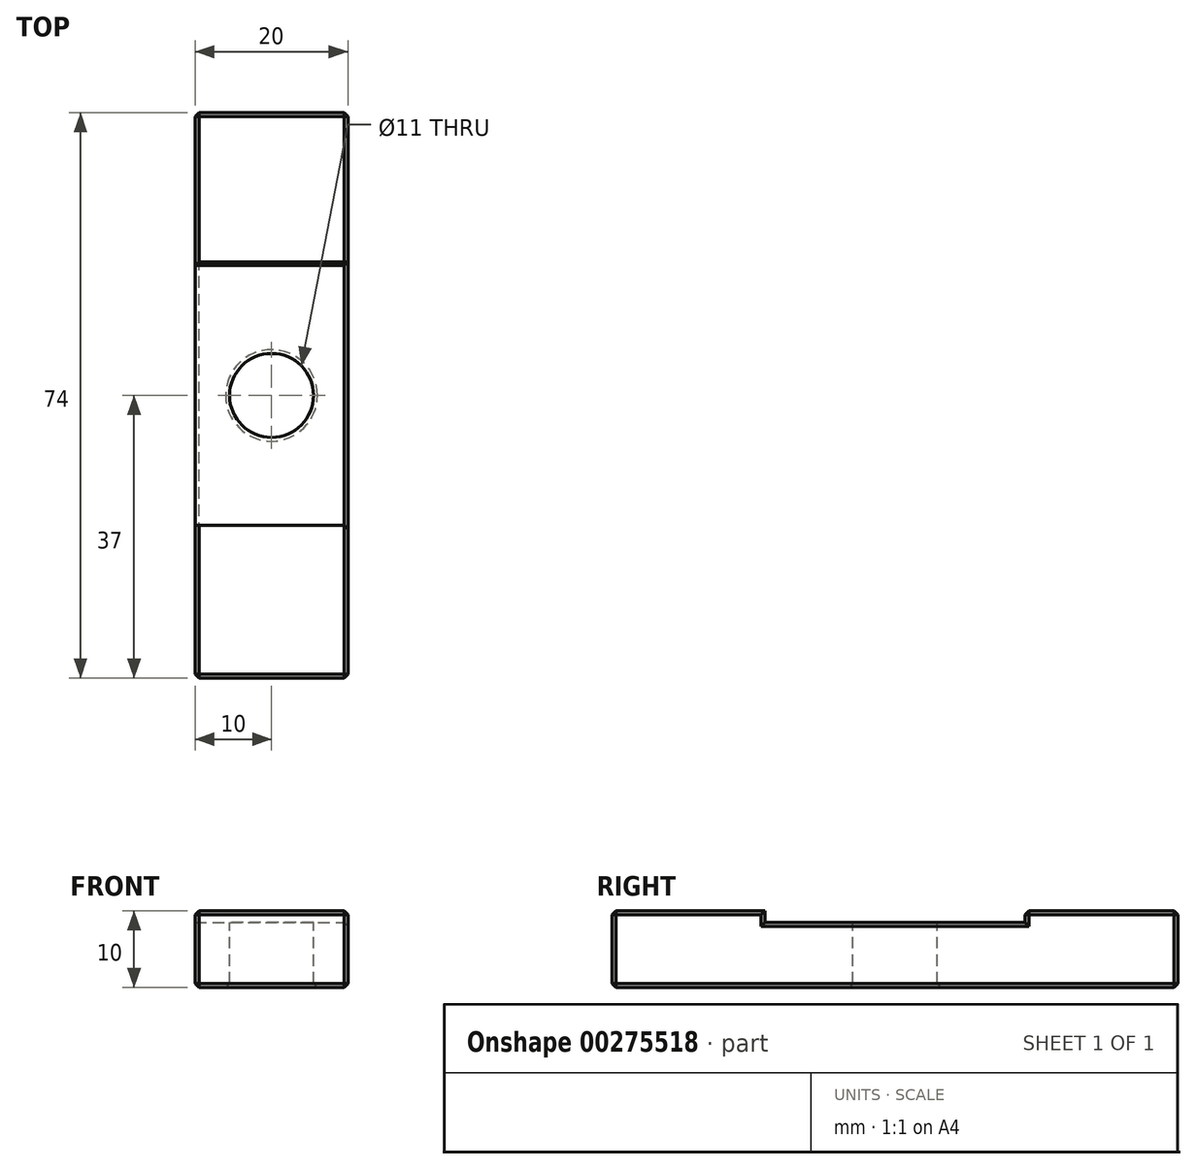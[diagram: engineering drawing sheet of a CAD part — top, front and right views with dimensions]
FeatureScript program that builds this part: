
annotation { "Feature Type Name" : "Feature", "Feature Type Description" : "" }
export const myFeature = defineFeature(function(context is Context, id is Id, definition is map)
    precondition{}
    {
        {
            var Q0;
            Q0=qCreatedBy(makeId("Top.planeOp"),FACE);
            var sketch = newSketch(context, id + "F0", { "sketchPlane" : qUnion([Q0])});
            skLineSegment(sketch, "E0.bottom", {"start": v(-10, -37) * mm, "end": v(10, -37) * mm});
            skLineSegment(sketch, "E0.top", {"start": v(-10, 37) * mm, "end": v(10, 37) * mm});
            skLineSegment(sketch, "E0.left", {"start": v(-10, -37) * mm, "end": v(-10, 37) * mm});
            skLineSegment(sketch, "E0.right", {"start": v(10, -37) * mm, "end": v(10, 37) * mm});
            skPoint(sketch, "E0.middle", {"position": v(0, 0) * mm});
            skSolve(sketch);
        }
        {
            var Q0;
            Q0 = qSketchRegion(id + "F0", true);
            extrude(context, id + "F1", {"entities" : qUnion([Q0]), "depth" : 10 * mm});
        }
        {
            var Q0;
            Q0=makeQuery(id+"F1.opExtrude","CAP_FACE",FACE,{"disambiguationData":[OSD([sQuery(id+"F0.wireOp",EDGE,"E0.bottom"),sQuery(id+"F0.wireOp",EDGE,"E0.top"),sQuery(id+"F0.wireOp",EDGE,"E0.left"),sQuery(id+"F0.wireOp",EDGE,"E0.right")])],"isStart":false});
            var sketch = newSketch(context, id + "F2", { "sketchPlane" : qUnion([Q0])});
            skLineSegment(sketch, "E1.bottom", {"start": v(-10, 37) * mm, "end": v(10, 37) * mm});
            skLineSegment(sketch, "E1.top", {"start": v(-10, 17) * mm, "end": v(10, 17) * mm});
            skLineSegment(sketch, "E1.left", {"start": v(-10, 37) * mm, "end": v(-10, 17) * mm});
            skLineSegment(sketch, "E1.right", {"start": v(10, 37) * mm, "end": v(10, 17) * mm});
            skLineSegment(sketch, "E2.bottom", {"start": v(10, -37) * mm, "end": v(-10, -37) * mm});
            skLineSegment(sketch, "E2.top", {"start": v(10, -17) * mm, "end": v(-10, -17) * mm});
            skLineSegment(sketch, "E2.left", {"start": v(10, -37) * mm, "end": v(10, -17) * mm});
            skLineSegment(sketch, "E2.right", {"start": v(-10, -37) * mm, "end": v(-10, -17) * mm});
            skSolve(sketch);
        }
        {
            var Q0;
            {var subQ0=sQuery(id+"F2.wireOp",EDGE,"E1.top");Q0=makeQuery(id+"F2.imprint","IMPRINT",FACE,{"disambiguationData":[TD([[makeQuery(id+"F2.imprint","IMPRINT",EDGE,{"derivedFrom":subQ0}),-1.0]])]});}
            extrude(context, id + "F3", {"entities" : qUnion([Q0]), "operationType" : NewBodyOperationType.REMOVE, "oppositeDirection" : true, "depth" : 1.5 * mm});
        }
        {
            var Q0;
            Q0=makeQuery(id+"F3.boolean.opBoolean","COPY",FACE,{"derivedFrom":makeQuery(id+"F3.opExtrude","CAP_FACE",FACE,{"disambiguationData":[OSD([sQuery(id+"F0.wireOp",EDGE,"E0.left"),sQuery(id+"F0.wireOp",EDGE,"E0.right"),sQuery(id+"F2.wireOp",EDGE,"E1.top"),sQuery(id+"F2.wireOp",EDGE,"E2.top")])],"isStart":false})});
            var sketch = newSketch(context, id + "F4", { "sketchPlane" : qUnion([Q0])});
            skCircle(sketch, "E3", {"center": v(0, 0) * mm, "radius": 5.5 * mm});
            skSolve(sketch);
        }
        {
            var Q0;
            Q0 = qSketchRegion(id + "F4", true);
            extrude(context, id + "F5", {"entities" : qUnion([Q0]), "operationType" : NewBodyOperationType.REMOVE, "endBound" : BoundingType.THROUGH_ALL, "oppositeDirection" : true, "depth" : 25 * mm});
        }
        {
            var Q0;
            Q0=makeQuery(id+"F5.boolean.opBoolean","COPY",EDGE,{"derivedFrom":makeQuery(id+"F5.opExtrude","CAP_EDGE",EDGE,{"disambiguationData":[OSD([sQuery(id+"F4.wireOp",EDGE,"E3")])],"isStart":true})});
            var Q1;
            Q1=makeQuery(id+"F1.opExtrude","SWEPT_EDGE",EDGE,{"disambiguationData":[OSD([sQuery(id+"F0.wireOp",EDGE,"E0.bottom"),sQuery(id+"F0.wireOp",EDGE,"E0.right")])]});
            var Q2;
            Q2=makeQuery(id+"F1.opExtrude","SWEPT_EDGE",EDGE,{"disambiguationData":[OSD([sQuery(id+"F0.wireOp",EDGE,"E0.bottom"),sQuery(id+"F0.wireOp",EDGE,"E0.left")])]});
            var Q3;
            Q3=makeQuery(id+"F1.opExtrude","SWEPT_EDGE",EDGE,{"disambiguationData":[OSD([sQuery(id+"F0.wireOp",EDGE,"E0.top"),sQuery(id+"F0.wireOp",EDGE,"E0.right")])]});
            var Q4;
            Q4=makeQuery(id+"F1.opExtrude","SWEPT_EDGE",EDGE,{"disambiguationData":[OSD([sQuery(id+"F0.wireOp",EDGE,"E0.top"),sQuery(id+"F0.wireOp",EDGE,"E0.left")])]});
            var Q5;
            Q5=makeQuery(id+"F1.opExtrude","CAP_EDGE",EDGE,{"disambiguationData":[OSD([sQuery(id+"F0.wireOp",EDGE,"E0.left")])],"isStart":true});
            var Q6;
            Q6=makeQuery(id+"F1.opExtrude","CAP_EDGE",EDGE,{"disambiguationData":[OSD([sQuery(id+"F0.wireOp",EDGE,"E0.bottom")])],"isStart":true});
            var Q7;
            Q7=makeQuery(id+"F1.opExtrude","CAP_EDGE",EDGE,{"disambiguationData":[OSD([sQuery(id+"F0.wireOp",EDGE,"E0.right")])],"isStart":true});
            var Q8;
            Q8=makeQuery(id+"F1.opExtrude","CAP_EDGE",EDGE,{"disambiguationData":[OSD([sQuery(id+"F0.wireOp",EDGE,"E0.top")])],"isStart":true});
            var Q9;
            {var subQ0=sQuery(id+"F0.wireOp",EDGE,"E0.right");var subQ1=sQuery(id+"F0.wireOp",EDGE,"E0.top");Q9=makeQuery(id+"F3.boolean.opBoolean","SPLIT",EDGE,{"disambiguationData":[TD([makeQuery(id+"F1.opExtrude","SWEPT_FACE",FACE,{"disambiguationData":[OSD([subQ1])]})])],"derivedFrom":makeQuery(id+"F1.opExtrude","CAP_EDGE",EDGE,{"disambiguationData":[OSD([subQ0])],"isStart":false})});}
            var Q10;
            {var subQ0=sQuery(id+"F0.wireOp",EDGE,"E0.left");var subQ1=sQuery(id+"F0.wireOp",EDGE,"E0.top");Q10=makeQuery(id+"F3.boolean.opBoolean","SPLIT",EDGE,{"disambiguationData":[TD([makeQuery(id+"F1.opExtrude","SWEPT_FACE",FACE,{"disambiguationData":[OSD([subQ1])]})])],"derivedFrom":makeQuery(id+"F1.opExtrude","CAP_EDGE",EDGE,{"disambiguationData":[OSD([subQ0])],"isStart":false})});}
            var Q11;
            {var subQ0=sQuery(id+"F0.wireOp",EDGE,"E0.bottom");var subQ1=sQuery(id+"F0.wireOp",EDGE,"E0.left");Q11=makeQuery(id+"F3.boolean.opBoolean","SPLIT",EDGE,{"disambiguationData":[TD([makeQuery(id+"F1.opExtrude","SWEPT_FACE",FACE,{"disambiguationData":[OSD([subQ0])]})])],"derivedFrom":makeQuery(id+"F1.opExtrude","CAP_EDGE",EDGE,{"disambiguationData":[OSD([subQ1])],"isStart":false})});}
            var Q12;
            {var subQ0=sQuery(id+"F0.wireOp",EDGE,"E0.bottom");var subQ1=sQuery(id+"F0.wireOp",EDGE,"E0.right");Q12=makeQuery(id+"F3.boolean.opBoolean","SPLIT",EDGE,{"disambiguationData":[TD([makeQuery(id+"F1.opExtrude","SWEPT_FACE",FACE,{"disambiguationData":[OSD([subQ0])]})])],"derivedFrom":makeQuery(id+"F1.opExtrude","CAP_EDGE",EDGE,{"disambiguationData":[OSD([subQ1])],"isStart":false})});}
            var Q13;
            Q13=makeQuery(id+"F3.boolean.opBoolean","COPY",EDGE,{"derivedFrom":makeQuery(id+"F3.opExtrude","CAP_EDGE",EDGE,{"disambiguationData":[OSD([sQuery(id+"F0.wireOp",EDGE,"E0.right")])],"isStart":false})});
            var Q14;
            Q14=makeQuery(id+"F3.boolean.opBoolean","COPY",EDGE,{"derivedFrom":makeQuery(id+"F3.opExtrude","CAP_EDGE",EDGE,{"disambiguationData":[OSD([sQuery(id+"F0.wireOp",EDGE,"E0.left")])],"isStart":false})});
            var Q15;
            Q15=makeQuery(id+"F1.opExtrude","CAP_EDGE",EDGE,{"disambiguationData":[OSD([sQuery(id+"F0.wireOp",EDGE,"E0.top")])],"isStart":false});
            var Q16;
            Q16=makeQuery(id+"F1.opExtrude","CAP_EDGE",EDGE,{"disambiguationData":[OSD([sQuery(id+"F0.wireOp",EDGE,"E0.bottom")])],"isStart":false});
            var Q17;
            Q17=makeQuery(id+"F5.boolean.opBoolean","INTERSECT",EDGE,{"derivedFrom":[makeQuery(id+"F1.opExtrude","CAP_FACE",FACE,{"disambiguationData":[OSD([sQuery(id+"F0.wireOp",EDGE,"E0.bottom"),sQuery(id+"F0.wireOp",EDGE,"E0.top"),sQuery(id+"F0.wireOp",EDGE,"E0.left"),sQuery(id+"F0.wireOp",EDGE,"E0.right")])],"isStart":true}),makeQuery(id+"F5.opExtrude","SWEPT_FACE",FACE,{"disambiguationData":[OSD([sQuery(id+"F4.wireOp",EDGE,"E3")])]})]});
            var Q18;
            Q18=makeQuery(id+"F3.boolean.opBoolean","COPY",EDGE,{"derivedFrom":makeQuery(id+"F3.opExtrude","CAP_EDGE",EDGE,{"disambiguationData":[OSD([sQuery(id+"F2.wireOp",EDGE,"E1.top")])],"isStart":true})});
            var Q19;
            Q19=makeQuery(id+"F3.boolean.opBoolean","COPY",EDGE,{"derivedFrom":makeQuery(id+"F3.opExtrude","CAP_EDGE",EDGE,{"disambiguationData":[OSD([sQuery(id+"F2.wireOp",EDGE,"E2.top")])],"isStart":true})});
            var Q20;
            Q20=makeQuery(id+"F3.boolean.opBoolean","COPY",EDGE,{"derivedFrom":makeQuery(id+"F3.opExtrude","SWEPT_EDGE",EDGE,{"disambiguationData":[OSD([sQuery(id+"F0.wireOp",EDGE,"E0.left"),sQuery(id+"F2.wireOp",EDGE,"E2.top"),sQuery(id+"F2.wireOp",EDGE,"E2.right")])]})});
            var Q21;
            Q21=makeQuery(id+"F3.boolean.opBoolean","COPY",EDGE,{"derivedFrom":makeQuery(id+"F3.opExtrude","SWEPT_EDGE",EDGE,{"disambiguationData":[OSD([sQuery(id+"F0.wireOp",EDGE,"E0.left"),sQuery(id+"F2.wireOp",EDGE,"E1.top"),sQuery(id+"F2.wireOp",EDGE,"E1.left")])]})});
            var Q22;
            Q22=makeQuery(id+"F3.boolean.opBoolean","COPY",EDGE,{"derivedFrom":makeQuery(id+"F3.opExtrude","SWEPT_EDGE",EDGE,{"disambiguationData":[OSD([sQuery(id+"F0.wireOp",EDGE,"E0.right"),sQuery(id+"F2.wireOp",EDGE,"E1.top"),sQuery(id+"F2.wireOp",EDGE,"E1.right")])]})});
            var Q23;
            Q23=makeQuery(id+"F1.opExtrude","SWEPT_FACE",FACE,{"disambiguationData":[OSD([sQuery(id+"F0.wireOp",EDGE,"E0.right")])]});
            chamfer(context, id + "F6", {"entities" : qUnion([Q0, Q1, Q2, Q3, Q4, Q5, Q6, Q7, Q8, Q9, Q10, Q11, Q12, Q13, Q14, Q15, Q16, Q17, Q18, Q19, Q20, Q21, Q22, Q23]), "width" : 0.5 * mm, "tangentPropagation" : true});
        }
    });
